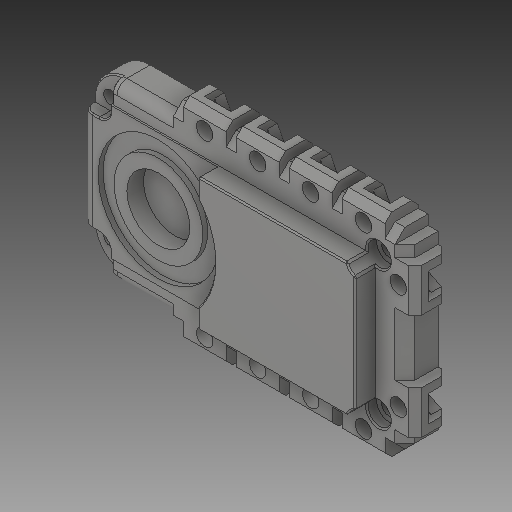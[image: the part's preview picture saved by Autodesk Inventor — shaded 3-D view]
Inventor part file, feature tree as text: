
AUTODESK INVENTOR PART (.ipt)
format: ipt  version: 2018 (Build 220112000, 112)  size: 391,168 bytes
history: native  units: mm
features: other x1, chamfer x1
ambient origin geometry x8: Origin, YZ Plane, XZ Plane, XY Plane, X Axis, Y Axis, Z Axis, Center Point
bodies: Body1 (feature_tree)
feature tree (2):
  other  "Твердое тело1"
  chamfer  "Chamfer3"  [1 undecoded]
note: 1 required parameter value undecoded (feature->parameter linkage not recoverable at this tier; creation-order binding heuristic only, values carry confidence <= 0.55)
